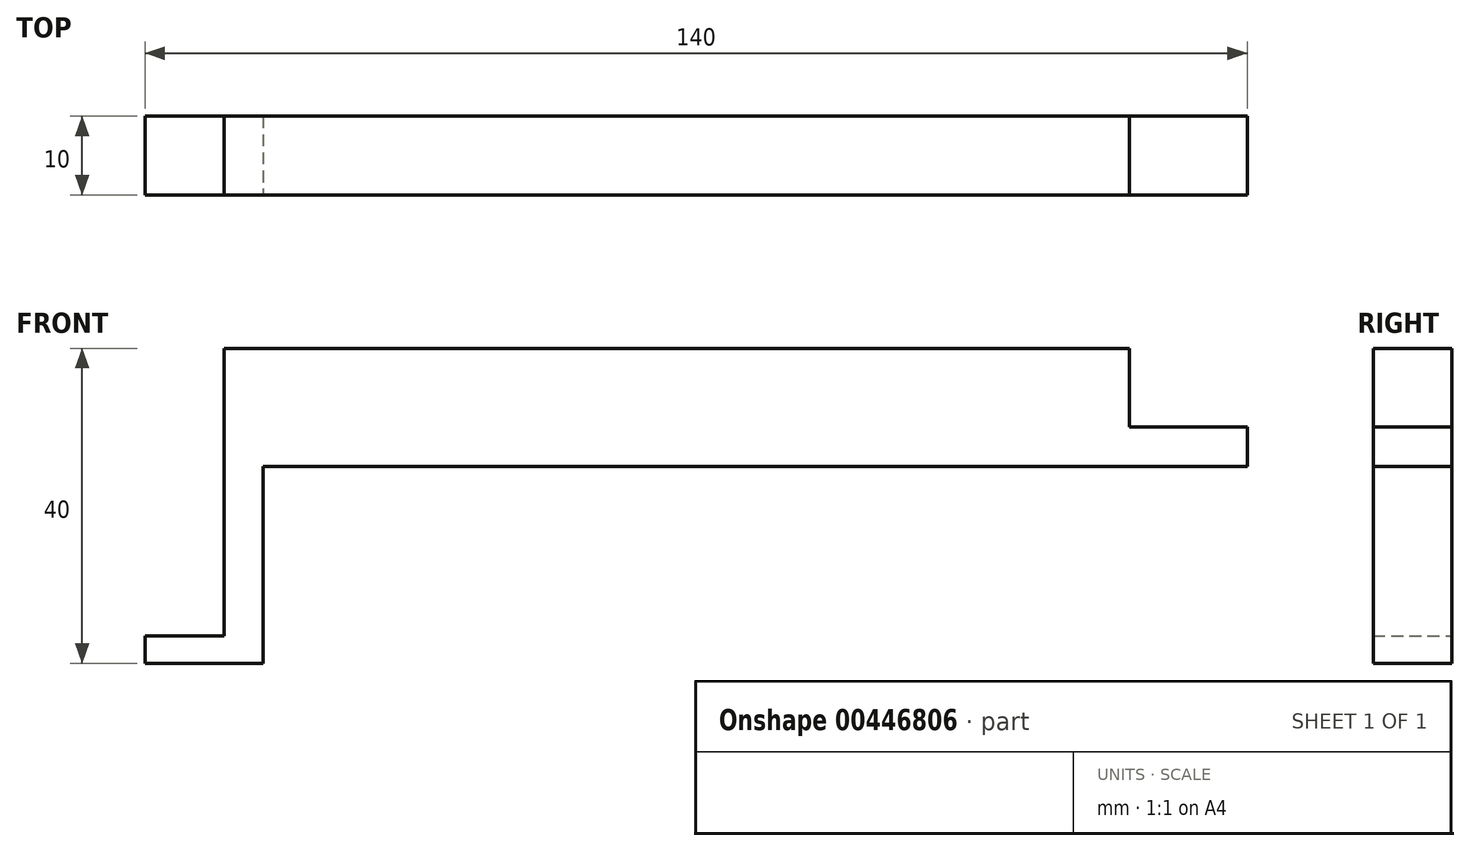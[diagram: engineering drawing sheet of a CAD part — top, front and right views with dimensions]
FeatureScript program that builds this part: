
annotation { "Feature Type Name" : "Feature", "Feature Type Description" : "" }
export const myFeature = defineFeature(function(context is Context, id is Id, definition is map)
    precondition{}
    {
        {
            var Q0;
            Q0=qCreatedBy(makeId("Front.planeOp"),FACE);
            var sketch = newSketch(context, id + "F0", { "sketchPlane" : qUnion([Q0])});
            skLineSegment(sketch, "E0.bottom", {"start": v(-57.5, 7.5) * mm, "end": v(57.5, 7.5) * mm});
            skLineSegment(sketch, "E0.top", {"start": v(-57.5, -7.5) * mm, "end": v(57.5, -7.5) * mm});
            skLineSegment(sketch, "E0.left", {"start": v(-57.5, 7.5) * mm, "end": v(-57.5, -7.5) * mm});
            skLineSegment(sketch, "E0.right", {"start": v(57.5, 7.5) * mm, "end": v(57.5, -7.5) * mm});
            skSolve(sketch);
        }
        {
            var Q0;
            Q0=qSketchRegion(id+"F0",true);
            extrude(context, id + "F1", {"entities" : qUnion([Q0]), "depth" : 10 * mm});
        }
        {
            var Q0;
            Q0=makeQuery(id+"F1.opExtrude","SWEPT_FACE",FACE,{"disambiguationData":[OSD([sQuery(id+"F0.wireOp",EDGE,"E0.bottom")])]});
            var sketch = newSketch(context, id + "F2", { "sketchPlane" : qUnion([Q0])});
            skLineSegment(sketch, "E1.bottom", {"start": v(57.5, 0) * mm, "end": v(42.5, 0) * mm});
            skLineSegment(sketch, "E1.top", {"start": v(57.5, -10) * mm, "end": v(42.5, -10) * mm});
            skLineSegment(sketch, "E1.left", {"start": v(57.5, 0) * mm, "end": v(57.5, -10) * mm});
            skLineSegment(sketch, "E1.right", {"start": v(42.5, 0) * mm, "end": v(42.5, -10) * mm});
            skSolve(sketch);
        }
        {
            var Q0;
            Q0=makeQuery(id+"F2.imprint","IMPRINT",FACE,{"disambiguationData":[TD([[makeQuery(id+"F2.imprint","IMPRINT",EDGE,{"derivedFrom":sQuery(id+"F2.wireOp",EDGE,"E1.bottom")}),-1.0]])]});
            extrude(context, id + "F3", {"entities" : qUnion([Q0]), "operationType" : NewBodyOperationType.REMOVE, "oppositeDirection" : true, "depth" : 10 * mm});
        }
        {
            var Q0;
            Q0=makeQuery(id+"F1.opExtrude","SWEPT_FACE",FACE,{"disambiguationData":[OSD([sQuery(id+"F0.wireOp",EDGE,"E0.top")])]});
            var sketch = newSketch(context, id + "F4", { "sketchPlane" : qUnion([Q0])});
            skLineSegment(sketch, "E2.bottom", {"start": v(-57.5, 0) * mm, "end": v(-52.5, 0) * mm});
            skLineSegment(sketch, "E2.top", {"start": v(-57.5, 10) * mm, "end": v(-52.5, 10) * mm});
            skLineSegment(sketch, "E2.left", {"start": v(-57.5, 0) * mm, "end": v(-57.5, 10) * mm});
            skLineSegment(sketch, "E2.right", {"start": v(-52.5, 0) * mm, "end": v(-52.5, 10) * mm});
            skSolve(sketch);
        }
        {
            var Q0;
            Q0=makeQuery(id+"F4.imprint","IMPRINT",FACE,{"disambiguationData":[TD([[makeQuery(id+"F4.imprint","IMPRINT",EDGE,{"derivedFrom":sQuery(id+"F4.wireOp",EDGE,"E2.bottom")}),1.0]])]});
            extrude(context, id + "F5", {"entities" : qUnion([Q0]), "operationType" : NewBodyOperationType.ADD, "depth" : 25 * mm});
        }
        {
            var Q0;
            Q0=makeQuery(id+"F5.boolean.opBoolean","MERGE",FACE,{"derivedFrom":[makeQuery(id+"F1.opExtrude","SWEPT_FACE",FACE,{"disambiguationData":[OSD([sQuery(id+"F0.wireOp",EDGE,"E0.left")])]}),makeQuery(id+"F5.opExtrude","SWEPT_FACE",FACE,{"disambiguationData":[OSD([sQuery(id+"F4.wireOp",EDGE,"E2.left")])]})]});
            var sketch = newSketch(context, id + "F6", { "sketchPlane" : qUnion([Q0])});
            skLineSegment(sketch, "E3.bottom", {"start": v(10, -32.5) * mm, "end": v(0, -32.5) * mm});
            skLineSegment(sketch, "E3.top", {"start": v(10, -29) * mm, "end": v(0, -29) * mm});
            skLineSegment(sketch, "E3.left", {"start": v(10, -32.5) * mm, "end": v(10, -29) * mm});
            skLineSegment(sketch, "E3.right", {"start": v(0, -32.5) * mm, "end": v(0, -29) * mm});
            skSolve(sketch);
        }
        {
            var Q0;
            Q0=makeQuery(id+"F6.imprint","IMPRINT",FACE,{"disambiguationData":[TD([[makeQuery(id+"F6.imprint","IMPRINT",EDGE,{"derivedFrom":sQuery(id+"F6.wireOp",EDGE,"E3.bottom")}),-1.0]])]});
            extrude(context, id + "F7", {"entities" : qUnion([Q0]), "operationType" : NewBodyOperationType.ADD, "depth" : 10 * mm});
        }
        {
            var Q0;
            Q0=makeQuery(id+"F1.opExtrude","SWEPT_FACE",FACE,{"disambiguationData":[OSD([sQuery(id+"F0.wireOp",EDGE,"E0.right")])]});
            extrude(context, id + "F8", {"entities" : qUnion([Q0]), "operationType" : NewBodyOperationType.ADD, "depth" : 15 * mm});
        }
        {
            var Q0;
            Q0=makeQuery(id+"F3.boolean.opBoolean","COPY",FACE,{"derivedFrom":makeQuery(id+"F3.opExtrude","SWEPT_FACE",FACE,{"disambiguationData":[OSD([sQuery(id+"F2.wireOp",EDGE,"E1.right")])]})});
            extrude(context, id + "F9", {"entities" : qUnion([Q0]), "operationType" : NewBodyOperationType.ADD, "depth" : 15 * mm});
        }
    });
